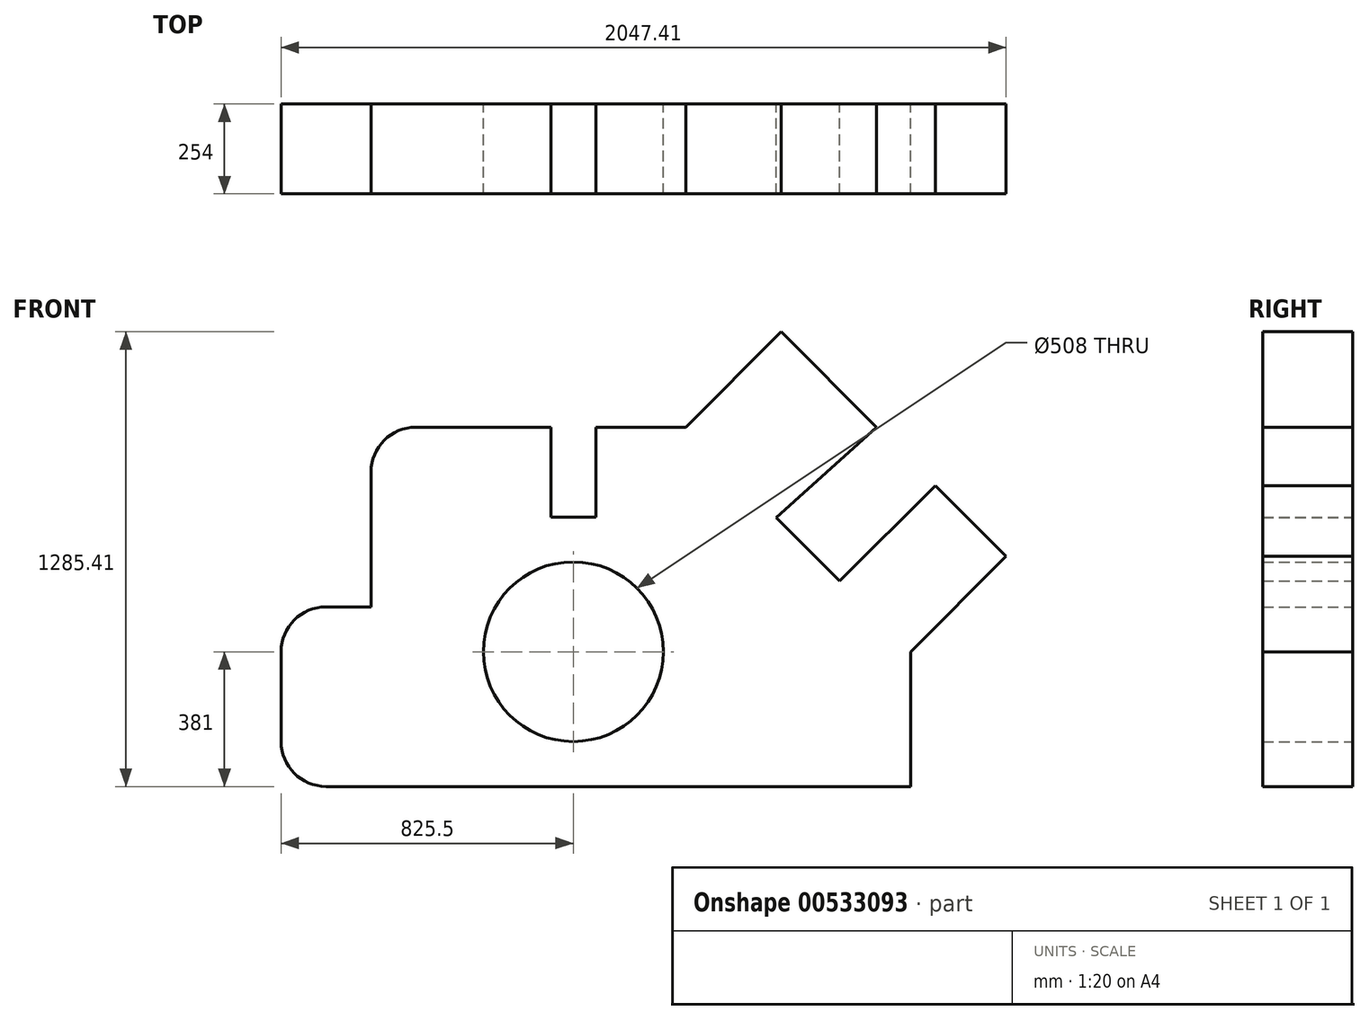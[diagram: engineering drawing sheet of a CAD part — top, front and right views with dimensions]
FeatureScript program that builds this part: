
annotation { "Feature Type Name" : "Feature", "Feature Type Description" : "" }
export const myFeature = defineFeature(function(context is Context, id is Id, definition is map)
    precondition{}
    {
        {
            var Q0;
            Q0=qCreatedBy(makeId("Front.planeOp"),FACE);
            var sketch = newSketch(context, id + "F0", { "sketchPlane" : qUnion([Q0])});
            skLineSegment(sketch, "E0", {"start": v(127, 0) * mm, "end": v(1778, 0) * mm});
            skLineSegment(sketch, "E1", {"start": v(1778, 0) * mm, "end": v(1778, 381) * mm});
            skLineSegment(sketch, "E2", {"start": v(0, 127) * mm, "end": v(0, 381) * mm});
            skCircle(sketch, "E3", {"center": v(825.5, 381) * mm, "radius": 254 * mm});
            skPoint(sketch, "E4.visualSharp", {"position": v(0, 0) * mm});
            skArc(sketch, "E4.filletArc", {"start": v(0, 127) * mm, "mid": v(37.2, 37.2) * mm, "end": v(127, 0) * mm});
            skLineSegment(sketch, "E5", {"start": v(127, 508) * mm, "end": v(254, 508) * mm});
            skPoint(sketch, "E6.visualSharp", {"position": v(0, 508) * mm});
            skArc(sketch, "E6.filletArc", {"start": v(127, 508) * mm, "mid": v(37.2, 470.8) * mm, "end": v(0, 381) * mm});
            skLineSegment(sketch, "E7", {"start": v(254, 508) * mm, "end": v(254, 889) * mm});
            skLineSegment(sketch, "E8", {"start": v(381, 1016) * mm, "end": v(762, 1016) * mm});
            skLineSegment(sketch, "E9", {"start": v(762, 1016) * mm, "end": v(762, 762) * mm});
            skLineSegment(sketch, "E10", {"start": v(762, 762) * mm, "end": v(889, 762) * mm});
            skLineSegment(sketch, "E11", {"start": v(889, 762) * mm, "end": v(889, 1016) * mm});
            skLineSegment(sketch, "E12", {"start": v(1778, 381) * mm, "end": v(2047.4, 650.4) * mm});
            skLineSegment(sketch, "E13", {"start": v(2047.4, 650.4) * mm, "end": v(1847.64, 850.18) * mm});
            skLineSegment(sketch, "E14", {"start": v(1847.64, 850.18) * mm, "end": v(1578.23, 580.77) * mm});
            skLineSegment(sketch, "E15", {"start": v(1578.23, 580.77) * mm, "end": v(1398.62, 760.38) * mm});
            skLineSegment(sketch, "E16", {"start": v(1398.62, 760.38) * mm, "end": v(1681.46, 1015.65) * mm});
            skLineSegment(sketch, "E17", {"start": v(889, 1016) * mm, "end": v(1143, 1016) * mm});
            skLineSegment(sketch, "E18", {"start": v(1143, 1016) * mm, "end": v(1412.4, 1285.4) * mm});
            skLineSegment(sketch, "E19", {"start": v(1412.4, 1285.4) * mm, "end": v(1681.46, 1015.65) * mm});
            skPoint(sketch, "E20.visualSharp", {"position": v(254, 1016) * mm});
            skArc(sketch, "E20.filletArc", {"start": v(381, 1016) * mm, "mid": v(291.2, 978.8) * mm, "end": v(254, 889) * mm});
            skSolve(sketch);
        }
        {
            var Q0;
            Q0=makeQuery(id+"F0.imprint","IMPRINT",FACE,{"disambiguationData":[TD([[makeQuery(id+"F0.imprint","IMPRINT",EDGE,{"derivedFrom":sQuery(id+"F0.wireOp",EDGE,"E0")}),1.0]])]});
            extrude(context, id + "F1", {"entities" : qUnion([Q0]), "depth" : 254 * mm, "offsetDistance" : 25.4 * mm});
        }
    });
